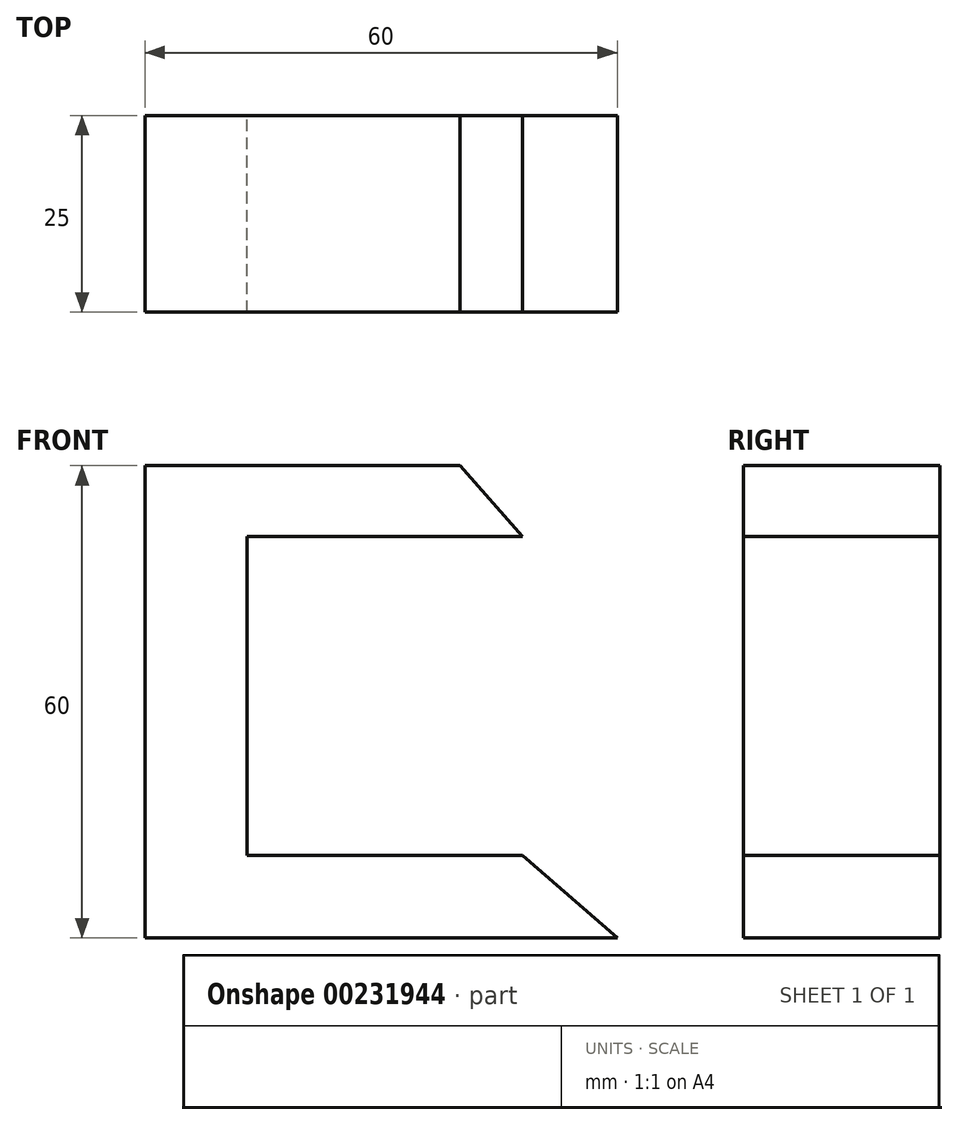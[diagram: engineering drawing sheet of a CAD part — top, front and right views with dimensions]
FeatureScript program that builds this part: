
annotation { "Feature Type Name" : "Feature", "Feature Type Description" : "" }
export const myFeature = defineFeature(function(context is Context, id is Id, definition is map)
    precondition{}
    {
        {
            var Q0;
            Q0=qCreatedBy(makeId("Front.planeOp"),FACE);
            var sketch = newSketch(context, id + "F0", { "sketchPlane" : qUnion([Q0])});
            skLineSegment(sketch, "E0", {"start": v(-24.34, 27.07) * mm, "end": v(15.66, 27.07) * mm});
            skLineSegment(sketch, "E1", {"start": v(-24.34, 27.07) * mm, "end": v(-24.34, -32.93) * mm});
            skLineSegment(sketch, "E2", {"start": v(-24.34, -32.93) * mm, "end": v(35.66, -32.93) * mm});
            skLineSegment(sketch, "E3", {"start": v(35.66, -32.93) * mm, "end": v(23.6, -22.4) * mm});
            skLineSegment(sketch, "E4", {"start": v(23.6, -22.4) * mm, "end": v(-11.4, -22.4) * mm});
            skLineSegment(sketch, "E5", {"start": v(-11.4, -22.4) * mm, "end": v(-11.4, 18.08) * mm});
            skLineSegment(sketch, "E6", {"start": v(-11.4, 18.08) * mm, "end": v(23.6, 18.08) * mm});
            skLineSegment(sketch, "E7", {"start": v(15.66, 27.07) * mm, "end": v(23.6, 18.08) * mm});
            skLineSegment(sketch, "E8", {"start": v(-24.34, 0) * mm, "end": v(-24.34, -2.93) * mm});
            skPoint(sketch, "E8.startSnap0", {"position": v(-24.34, -2.93) * mm});
            skSolve(sketch);
        }
        {
            var Q0;
            Q0 = qSketchRegion(id + "F0", true);
            extrude(context, id + "F1", {"entities" : qUnion([Q0]), "depth" : 25 * mm});
        }
    });
